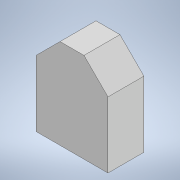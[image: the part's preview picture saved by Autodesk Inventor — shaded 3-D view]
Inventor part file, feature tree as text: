
AUTODESK INVENTOR PART (.ipt)
format: ipt  version: 2021 (Build 250183000, 183)  size: 96,256 bytes
history: native  units: in
note: dims shown in document units (in); Inventor stores cm internally (conversion verified against a paired STEP export)
features: extrude x1, sketch x1
ambient origin geometry x8: Origin, YZ Plane, XZ Plane, XY Plane, X Axis, Y Axis, Z Axis, Center Point
bodies: Solid1 (feature_tree)
feature tree (2):
  extrude  "Extrusion1"  Depth=0.2362in
  sketch  "Sketch1"  dims[d0=0.2362in d1=0.4331in d2=0.2362in d3=0.4331in d4=0.5906in d5=0.0787in d6=0.0787in d7=0.2362in d8=0.0in]
